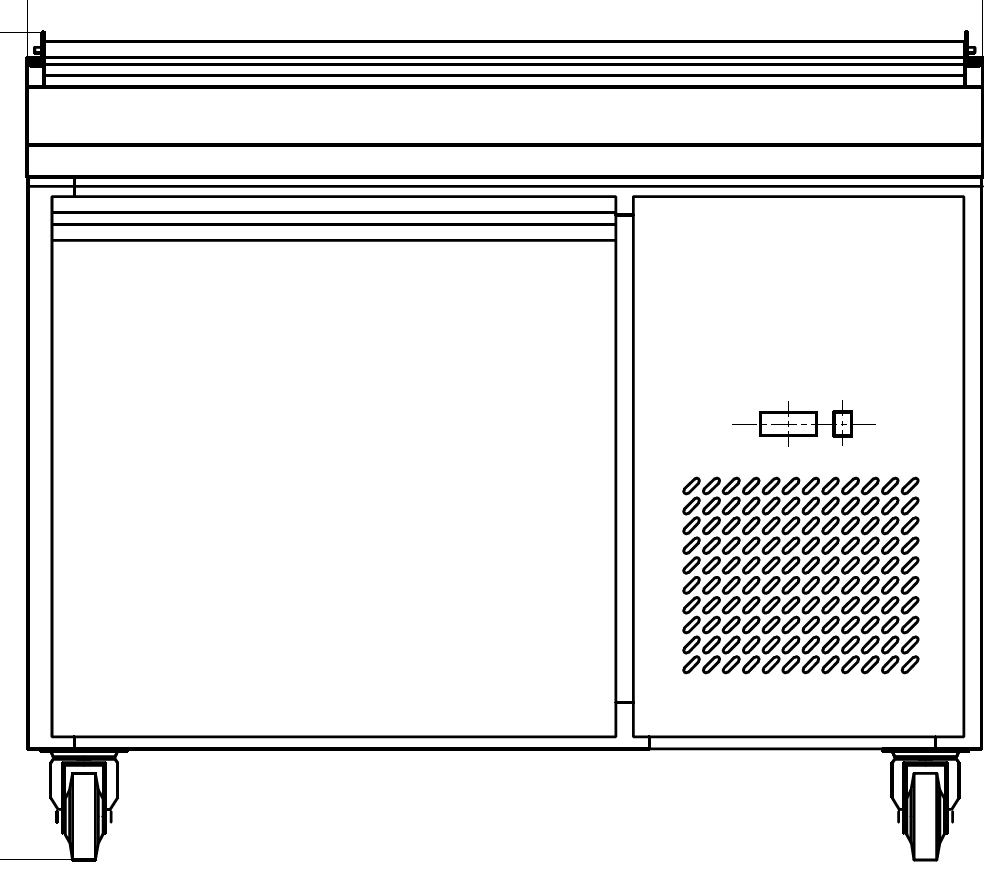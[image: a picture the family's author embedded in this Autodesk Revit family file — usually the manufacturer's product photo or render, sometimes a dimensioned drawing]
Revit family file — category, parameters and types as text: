
# Revit family: QF_Kelvinator_738252_KCHPT50.6_1-Door_Pizza_Prep_Table_48_Long
name_source: partatom
category: Specialty Equipment
units: mm (PartAtom-declared; Revit-internal decimal feet)

## family parameters
Always vertical = Yes
Cut with Voids When Loaded = No
Part Type = Normal
Room Calculation Point = No
Round Connector Dimension = Use Diameter
Shared = No
Work Plane-Based = No

## types (1)
- QF_Kelvinator_738252_KCHPT50.6_1-Door_Pizza_Prep_Table_48_Long
    Apparent Power = 0 VA
    Conn Conduit = Yes
    Conn Plug = 5-15P
    Cycle = 60 Hz
    Default Elevation = 0 "
    Depth = 32.25 "
    Description = 1-Door Pizza Prep Table 48" Long
    Elec Conn Connection Height = 0 "
    Elec Conn RI Height = 0 "
    FL Amps = 5 A
    Foodservice Equipment Identifier = Yes
    HP = 1/3
    Height = 41.313 "
    Identify Quantity as Lot = Yes
    Item Number = 738252
    Length = 47.375 "
    Manufacturer = Kelvinator Commercial
    Max Overcurrent Protection = 0 A
    Min Ckt Ampacity = 0 A
    Model = 738252 (KCHPT50.6)
    Number of Poles = 1
    Phase = 1
    Refrigerant Type = R290
    Volts = 115 V
    Watts = 700 W
    Weight in Pounds = 224.872

## geometry (parser evidence)
native form markers: Sweep x5
no freeform markers — native parametric forms only
